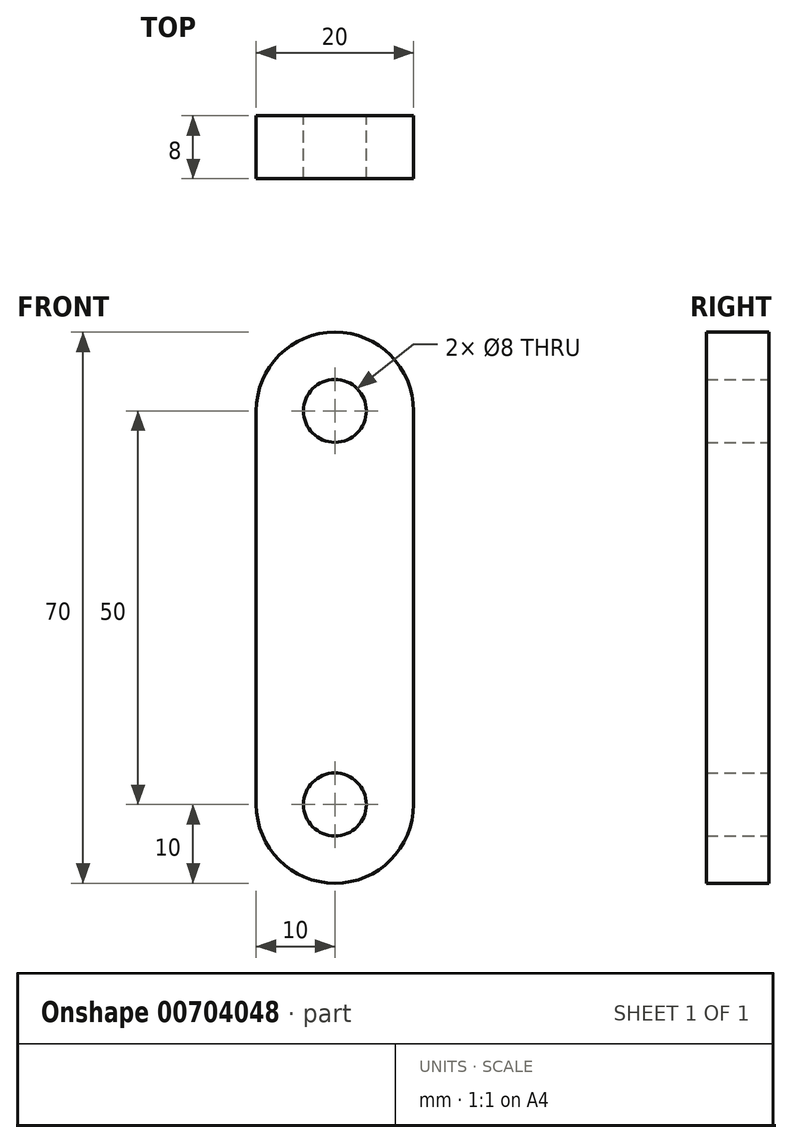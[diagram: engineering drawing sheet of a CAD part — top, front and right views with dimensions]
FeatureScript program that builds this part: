
annotation { "Feature Type Name" : "Feature", "Feature Type Description" : "" }
export const myFeature = defineFeature(function(context is Context, id is Id, definition is map)
    precondition{}
    {
        {
            var Q0;
            Q0=qCreatedBy(makeId("Front.planeOp"),FACE);
            var sketch = newSketch(context, id + "F0", { "sketchPlane" : qUnion([Q0])});
            skCircle(sketch, "E0", {"center": v(0, 0) * mm, "radius": 4 * mm});
            skArc(sketch, "E1", {"start": v(-10, 0) * mm, "mid": v(0, -10) * mm, "end": v(10, 0) * mm});
            skCircle(sketch, "E2", {"center": v(0, 50) * mm, "radius": 4 * mm});
            skArc(sketch, "E3", {"start": v(10, 50) * mm, "mid": v(0, 60) * mm, "end": v(-10, 50) * mm});
            skLineSegment(sketch, "E4", {"start": v(-10, 50) * mm, "end": v(-10, 0) * mm});
            skLineSegment(sketch, "E5", {"start": v(10, 0) * mm, "end": v(10, 50) * mm});
            skSolve(sketch);
        }
        {
            var Q0;
            Q0=makeQuery(id+"F0.imprint","IMPRINT",FACE,{"disambiguationData":[TD([[makeQuery(id+"F0.imprint","IMPRINT",EDGE,{"derivedFrom":sQuery(id+"F0.wireOp",EDGE,"E0")}),-1.0]])]});
            extrude(context, id + "F1", {"entities" : qUnion([Q0]), "depth" : 8 * mm, "offsetDistance" : 25.4 * mm});
        }
    });
